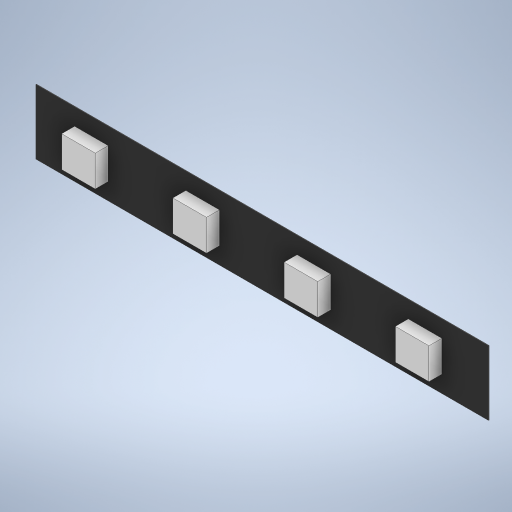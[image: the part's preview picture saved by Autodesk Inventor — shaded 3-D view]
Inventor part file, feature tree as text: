
AUTODESK INVENTOR PART (.ipt)
format: ipt  version: 2023 (Build 270158000, 158)  size: 287,232 bytes
history: native  units: mm
features: extrude x2, sketch x2, other x1
ambient origin geometry x8: Origin, YZ Plane, XZ Plane, XY Plane, X Axis, Y Axis, Z Axis, Center Point
bodies: Body1 (feature_tree)
feature tree (5):
  other  "솔리드1"
  extrude  "돌출1"  Depth=70.0mm
  extrude  "돌출2"  Depth=10.0mm
  sketch  "스케치1"
  sketch  "스케치2"
